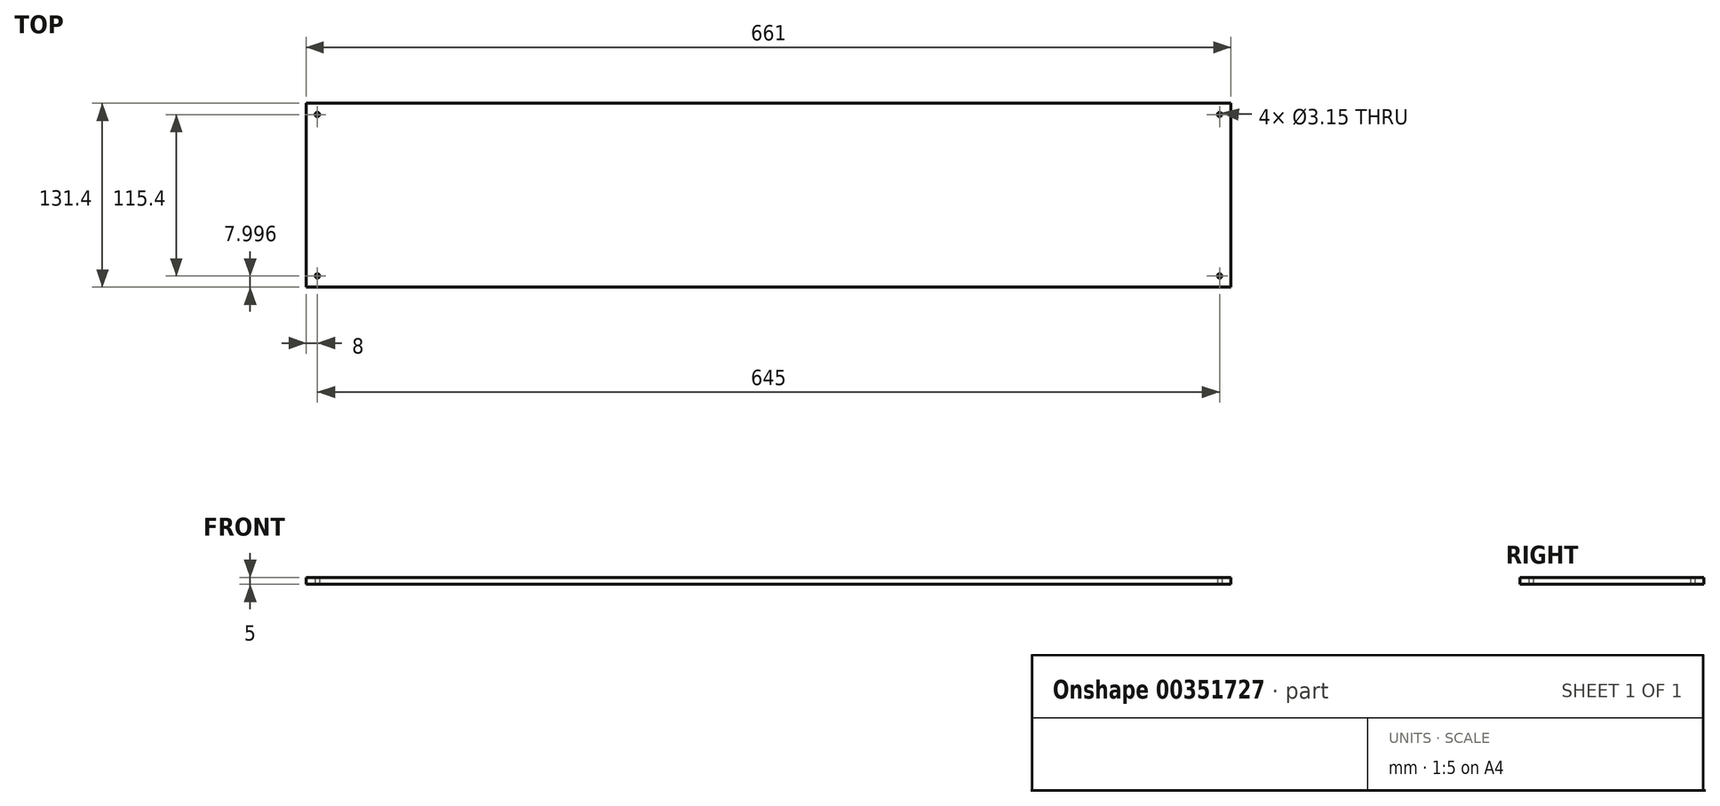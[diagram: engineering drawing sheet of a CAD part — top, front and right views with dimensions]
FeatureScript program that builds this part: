
annotation { "Feature Type Name" : "Feature", "Feature Type Description" : "" }
export const myFeature = defineFeature(function(context is Context, id is Id, definition is map)
    precondition{}
    {
        {
            var Q0;
            Q0=qCreatedBy(makeId("Top.planeOp"),FACE);
            var sketch = newSketch(context, id + "F0", { "sketchPlane" : qUnion([Q0])});
            skLineSegment(sketch, "E0.bottom", {"start": v(-550.19, 88.73) * mm, "end": v(110.81, 88.73) * mm});
            skLineSegment(sketch, "E0.top", {"start": v(-550.19, -42.67) * mm, "end": v(110.81, -42.67) * mm});
            skLineSegment(sketch, "E0.left", {"start": v(-550.19, 88.73) * mm, "end": v(-550.19, -42.67) * mm});
            skLineSegment(sketch, "E0.right", {"start": v(110.81, 88.73) * mm, "end": v(110.81, -42.67) * mm});
            skCircle(sketch, "E1", {"center": v(-542.19, 80.73) * mm, "radius": 1.57 * mm});
            skCircle(sketch, "E2", {"center": v(102.81, 80.73) * mm, "radius": 1.57 * mm});
            skCircle(sketch, "E3", {"center": v(102.81, -34.67) * mm, "radius": 1.57 * mm});
            skCircle(sketch, "E4", {"center": v(-542.19, -34.67) * mm, "radius": 1.57 * mm});
            skLineSegment(sketch, "E5", {"start": v(-542.19, 80.73) * mm, "end": v(102.81, 80.73) * mm, "construction": true});
            skLineSegment(sketch, "E6", {"start": v(102.81, 80.73) * mm, "end": v(102.81, -34.67) * mm, "construction": true});
            skLineSegment(sketch, "E7", {"start": v(102.81, -34.67) * mm, "end": v(-542.19, -34.67) * mm, "construction": true});
            skLineSegment(sketch, "E8", {"start": v(-542.19, -34.67) * mm, "end": v(-542.19, 80.73) * mm, "construction": true});
            skSolve(sketch);
        }
        {
            var Q0;
            Q0=makeQuery(id+"F0.imprint","IMPRINT",FACE,{"disambiguationData":[TD([[makeQuery(id+"F0.imprint","IMPRINT",EDGE,{"derivedFrom":sQuery(id+"F0.wireOp",EDGE,"E0.bottom")}),-1.0]])]});
            extrude(context, id + "F1", {"entities" : qUnion([Q0]), "depth" : 5 * mm});
        }
    });
